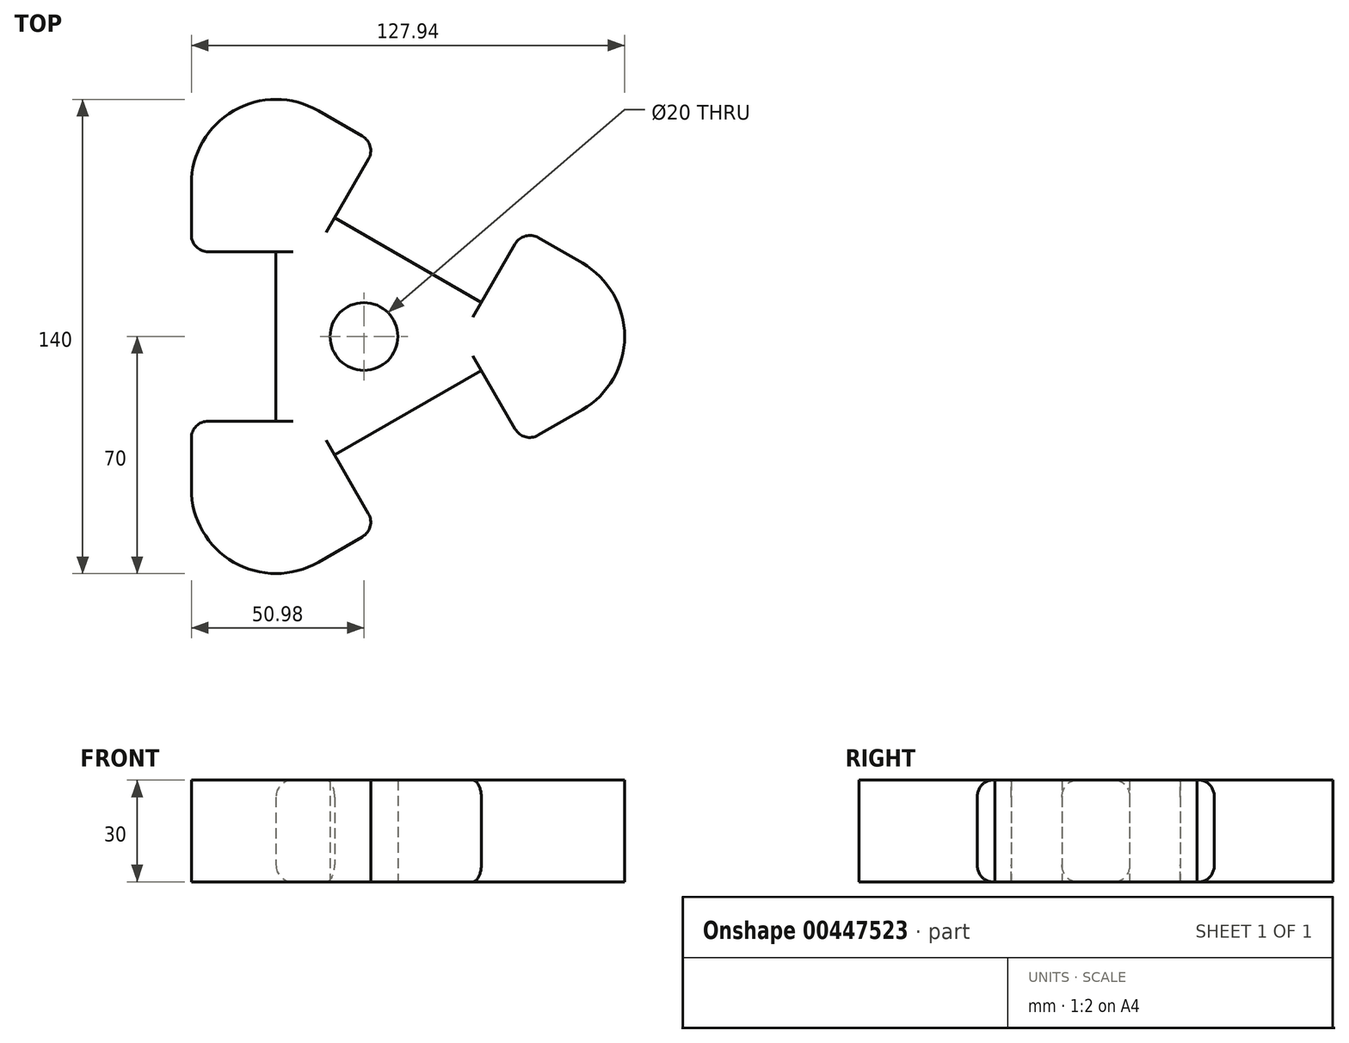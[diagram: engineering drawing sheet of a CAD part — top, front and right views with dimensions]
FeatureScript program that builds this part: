
annotation { "Feature Type Name" : "Feature", "Feature Type Description" : "" }
export const myFeature = defineFeature(function(context is Context, id is Id, definition is map)
    precondition{}
    {
        {
            var Q0;
            Q0=qCreatedBy(makeId("Top.planeOp"),FACE);
            var sketch = newSketch(context, id + "F0", { "sketchPlane" : qUnion([Q0])});
            skLineSegment(sketch, "E0.1", {"start": v(-8.66, 35) * mm, "end": v(34.64, 10) * mm});
            skPoint(sketch, "E0.0.midPoint", {"position": v(-25.98, 0) * mm});
            skLineSegment(sketch, "E1", {"start": v(-13.48, 66.65) * mm, "end": v(3.84, 56.65) * mm});
            skLineSegment(sketch, "E2", {"start": v(34.64, 10) * mm, "end": v(47.14, 31.65) * mm});
            skLineSegment(sketch, "E3", {"start": v(47.14, 31.65) * mm, "end": v(64.46, 21.65) * mm});
            skLineSegment(sketch, "E4", {"start": v(3.84, 56.65) * mm, "end": v(-8.66, 35) * mm});
            skLineSegment(sketch, "E5", {"start": v(-50.98, 45) * mm, "end": v(-50.98, 25) * mm});
            skLineSegment(sketch, "E6", {"start": v(-50.98, 25) * mm, "end": v(-25.98, 25) * mm});
            skLineSegment(sketch, "E7", {"start": v(-50.98, -45) * mm, "end": v(-50.98, -25) * mm});
            skLineSegment(sketch, "E8", {"start": v(-50.98, -25) * mm, "end": v(-25.98, -25) * mm});
            skLineSegment(sketch, "E9", {"start": v(-13.48, -66.65) * mm, "end": v(3.84, -56.65) * mm});
            skLineSegment(sketch, "E10", {"start": v(3.84, -56.65) * mm, "end": v(-8.66, -35) * mm});
            skLineSegment(sketch, "E11", {"start": v(64.46, -21.65) * mm, "end": v(47.14, -31.65) * mm});
            skLineSegment(sketch, "E12", {"start": v(47.14, -31.65) * mm, "end": v(34.64, -10) * mm});
            skArc(sketch, "E13", {"start": v(-50.98, -45) * mm, "mid": v(-38.48, -66.65) * mm, "end": v(-13.48, -66.65) * mm});
            skArc(sketch, "E14", {"start": v(-13.48, 66.65) * mm, "mid": v(-38.48, 66.65) * mm, "end": v(-50.98, 45) * mm});
            skArc(sketch, "E15", {"start": v(64.46, -21.65) * mm, "mid": v(76.96, 0) * mm, "end": v(64.46, 21.65) * mm});
            skLineSegment(sketch, "E16", {"start": v(-25.98, 25) * mm, "end": v(-25.98, -25) * mm});
            skLineSegment(sketch, "E17", {"start": v(-8.66, -35) * mm, "end": v(34.64, -10) * mm});
            skPoint(sketch, "E18", {"position": v(0, 0) * mm});
            skSolve(sketch);
        }
        {
            var Q0;
            Q0 = qSketchRegion(id + "F0", true);
            extrude(context, id + "F1", {"entities" : qUnion([Q0]), "endBound" : BoundingType.SYMMETRIC, "depth" : 30 * mm});
        }
        {
            var Q0;
            Q0=makeQuery(id+"F1.opExtrude","CAP_EDGE",EDGE,{"disambiguationData":[OSD([sQuery(id+"F0.wireOp",EDGE,"E0.1")])],"isStart":false});
            var Q1;
            Q1=makeQuery(id+"F1.opExtrude","CAP_EDGE",EDGE,{"disambiguationData":[OSD([sQuery(id+"F0.wireOp",EDGE,"E17")])],"isStart":false});
            var Q2;
            Q2=makeQuery(id+"F1.opExtrude","CAP_EDGE",EDGE,{"disambiguationData":[OSD([sQuery(id+"F0.wireOp",EDGE,"E16")])],"isStart":false});
            var Q3;
            Q3=makeQuery(id+"F1.opExtrude","CAP_EDGE",EDGE,{"disambiguationData":[OSD([sQuery(id+"F0.wireOp",EDGE,"E0.1")])],"isStart":true});
            var Q4;
            Q4=makeQuery(id+"F1.opExtrude","CAP_EDGE",EDGE,{"disambiguationData":[OSD([sQuery(id+"F0.wireOp",EDGE,"E17")])],"isStart":true});
            var Q5;
            Q5=makeQuery(id+"F1.opExtrude","CAP_EDGE",EDGE,{"disambiguationData":[OSD([sQuery(id+"F0.wireOp",EDGE,"E16")])],"isStart":true});
            var Q6;
            Q6=makeQuery(id+"F1.opExtrude","SWEPT_EDGE",EDGE,{"disambiguationData":[OSD([sQuery(id+"F0.wireOp",EDGE,"E1"),sQuery(id+"F0.wireOp",EDGE,"E4")])]});
            var Q7;
            Q7=makeQuery(id+"F1.opExtrude","SWEPT_EDGE",EDGE,{"disambiguationData":[OSD([sQuery(id+"F0.wireOp",EDGE,"E9"),sQuery(id+"F0.wireOp",EDGE,"E10")])]});
            var Q8;
            Q8=makeQuery(id+"F1.opExtrude","SWEPT_EDGE",EDGE,{"disambiguationData":[OSD([sQuery(id+"F0.wireOp",EDGE,"E11"),sQuery(id+"F0.wireOp",EDGE,"E12")])]});
            var Q9;
            Q9=makeQuery(id+"F1.opExtrude","SWEPT_EDGE",EDGE,{"disambiguationData":[OSD([sQuery(id+"F0.wireOp",EDGE,"E2"),sQuery(id+"F0.wireOp",EDGE,"E3")])]});
            var Q10;
            Q10=makeQuery(id+"F1.opExtrude","SWEPT_EDGE",EDGE,{"disambiguationData":[OSD([sQuery(id+"F0.wireOp",EDGE,"E7"),sQuery(id+"F0.wireOp",EDGE,"E8")])]});
            var Q11;
            Q11=makeQuery(id+"F1.opExtrude","SWEPT_EDGE",EDGE,{"disambiguationData":[OSD([sQuery(id+"F0.wireOp",EDGE,"E5"),sQuery(id+"F0.wireOp",EDGE,"E6")])]});
            fillet(context, id + "F2", {"entities" : qUnion([Q0, Q1, Q2, Q3, Q4, Q5, Q6, Q7, Q8, Q9, Q10, Q11]), "radius" : 5 * mm, "tangentPropagation" : true, "allowEdgeOverflow" : false});
        }
        {
            var Q0;
            Q0=sQuery(id+"F0.wireOp",VERTEX,"E18");
            var Q1;
            Q1=makeQuery(id+"F1.opExtrude","SWEPT_BODY",BODY,{"disambiguationData":[OSD([sQuery(id+"F0.wireOp",EDGE,"E0.1"),sQuery(id+"F0.wireOp",EDGE,"E1"),sQuery(id+"F0.wireOp",EDGE,"E2"),sQuery(id+"F0.wireOp",EDGE,"E3"),sQuery(id+"F0.wireOp",EDGE,"E4"),sQuery(id+"F0.wireOp",EDGE,"E5"),sQuery(id+"F0.wireOp",EDGE,"E6"),sQuery(id+"F0.wireOp",EDGE,"E7"),sQuery(id+"F0.wireOp",EDGE,"E8"),sQuery(id+"F0.wireOp",EDGE,"E9"),sQuery(id+"F0.wireOp",EDGE,"E10"),sQuery(id+"F0.wireOp",EDGE,"E11"),sQuery(id+"F0.wireOp",EDGE,"E12"),sQuery(id+"F0.wireOp",EDGE,"E13"),sQuery(id+"F0.wireOp",EDGE,"E14"),sQuery(id+"F0.wireOp",EDGE,"E15"),sQuery(id+"F0.wireOp",EDGE,"E16"),sQuery(id+"F0.wireOp",EDGE,"E17")])]});
            hole(context, id + "F3", {"style" : HoleStyle.SIMPLE, "endStyle" : HoleEndStyle.THROUGH, "oppositeDirection" : true, "holeDiameter" : 20 * mm, "isTappedThrough" : true, "tappedDepth" : 12 * mm, "tapClearance" : 3, "startFromSketch" : true, "locations" : qUnion([Q0]), "scope" : qUnion([Q1])});
        }
        {
            var Q0;
            Q0=sQuery(id+"F0.wireOp",VERTEX,"E18");
            var Q1;
            Q1=makeQuery(id+"F1.opExtrude","SWEPT_BODY",BODY,{"disambiguationData":[OSD([sQuery(id+"F0.wireOp",EDGE,"E0.1"),sQuery(id+"F0.wireOp",EDGE,"E1"),sQuery(id+"F0.wireOp",EDGE,"E2"),sQuery(id+"F0.wireOp",EDGE,"E3"),sQuery(id+"F0.wireOp",EDGE,"E4"),sQuery(id+"F0.wireOp",EDGE,"E5"),sQuery(id+"F0.wireOp",EDGE,"E6"),sQuery(id+"F0.wireOp",EDGE,"E7"),sQuery(id+"F0.wireOp",EDGE,"E8"),sQuery(id+"F0.wireOp",EDGE,"E9"),sQuery(id+"F0.wireOp",EDGE,"E10"),sQuery(id+"F0.wireOp",EDGE,"E11"),sQuery(id+"F0.wireOp",EDGE,"E12"),sQuery(id+"F0.wireOp",EDGE,"E13"),sQuery(id+"F0.wireOp",EDGE,"E14"),sQuery(id+"F0.wireOp",EDGE,"E15"),sQuery(id+"F0.wireOp",EDGE,"E16"),sQuery(id+"F0.wireOp",EDGE,"E17")])]});
            hole(context, id + "F4", {"style" : HoleStyle.SIMPLE, "endStyle" : HoleEndStyle.THROUGH, "holeDiameter" : 20 * mm, "isTappedThrough" : true, "tappedDepth" : 12 * mm, "tapClearance" : 3, "startFromSketch" : true, "locations" : qUnion([Q0]), "scope" : qUnion([Q1])});
        }
    });
